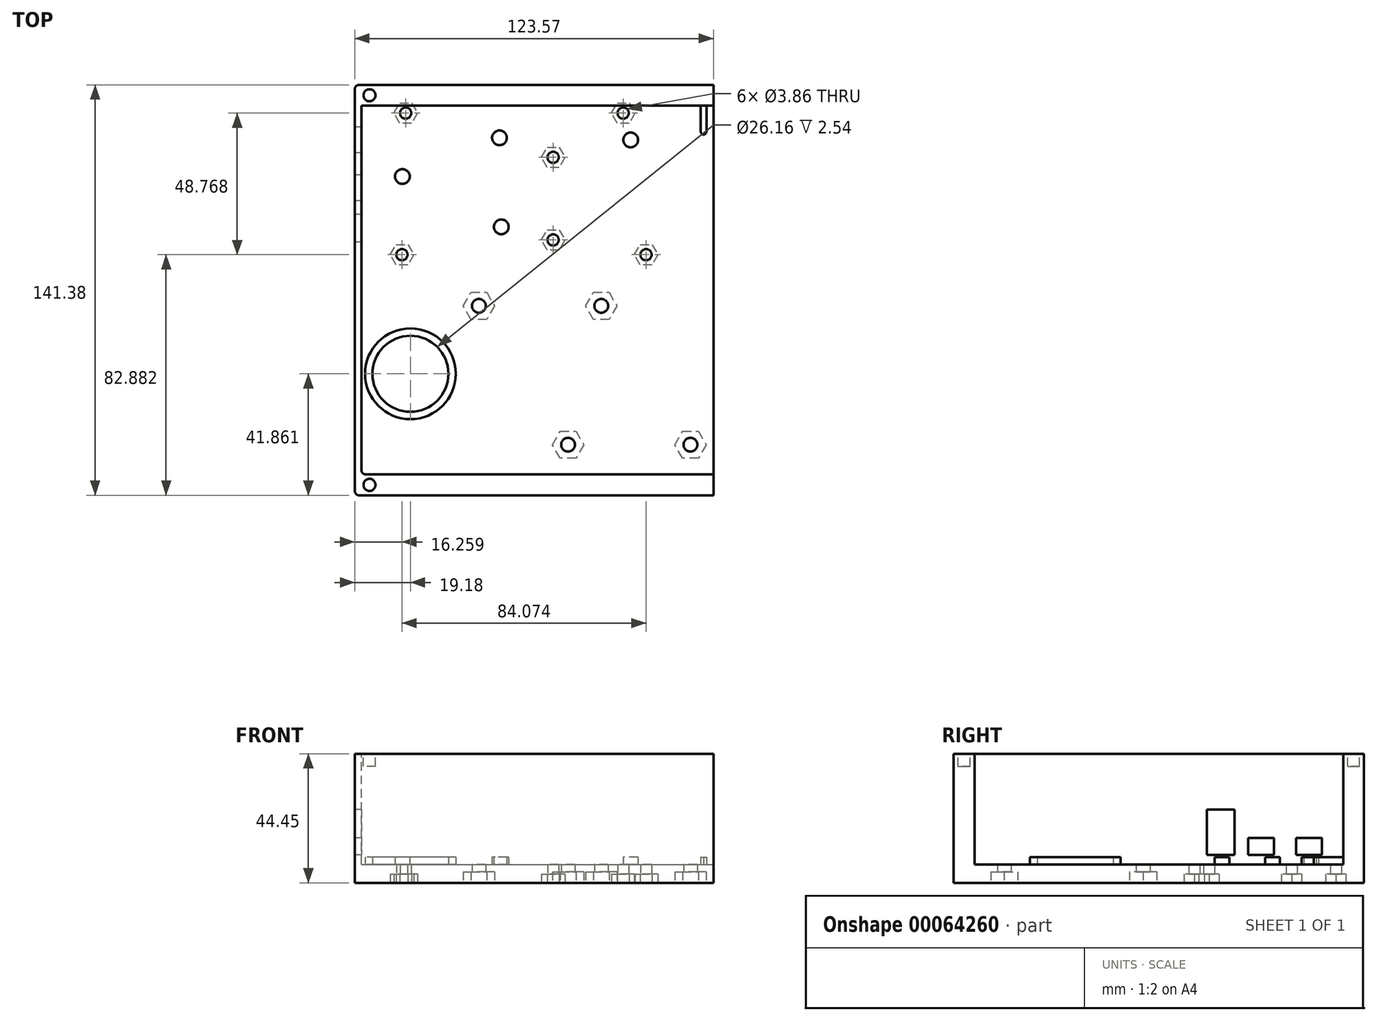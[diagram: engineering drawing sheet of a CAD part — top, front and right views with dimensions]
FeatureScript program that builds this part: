
annotation { "Feature Type Name" : "Feature", "Feature Type Description" : "" }
export const myFeature = defineFeature(function(context is Context, id is Id, definition is map)
    precondition{}
    {
        {
            var Q0;
            Q0=qCreatedBy(makeId("Top.planeOp"),FACE);
            var sketch = newSketch(context, id + "F0", { "sketchPlane" : qUnion([Q0])});
            skLineSegment(sketch, "E0.bottom", {"start": v(-98.88, 40.37) * mm, "end": v(3.23, 40.37) * mm});
            skLineSegment(sketch, "E0.top", {"start": v(-98.88, -13.48) * mm, "end": v(3.23, -13.48) * mm});
            skLineSegment(sketch, "E0.left", {"start": v(-98.88, 40.37) * mm, "end": v(-98.88, -13.48) * mm});
            skLineSegment(sketch, "E0.right", {"start": v(3.23, 40.37) * mm, "end": v(3.23, -13.48) * mm});
            skSolve(sketch);
        }
        {
            var Q0;
            Q0=qCreatedBy(makeId("Top.planeOp"),FACE);
            var sketch = newSketch(context, id + "F1", { "sketchPlane" : qUnion([Q0])});
            skLineSegment(sketch, "E1.bottom", {"start": v(-98.88, 40.37) * mm, "end": v(88.57, 40.37) * mm});
            skLineSegment(sketch, "E1.top", {"start": v(-98.88, -86.63) * mm, "end": v(88.57, -86.63) * mm});
            skLineSegment(sketch, "E1.left", {"start": v(-98.88, 40.37) * mm, "end": v(-98.88, -86.63) * mm});
            skLineSegment(sketch, "E1.right", {"start": v(88.57, 40.37) * mm, "end": v(88.57, -86.63) * mm});
            skSolve(sketch);
        }
        {
            var Q0;
            Q0=qCreatedBy(makeId("Top.planeOp"),FACE);
            var sketch = newSketch(context, id + "F2", { "sketchPlane" : qUnion([Q0])});
            skLineSegment(sketch, "E2", {"start": v(5.77, 40.37) * mm, "end": v(5.77, 30.21) * mm});
            skLineSegment(sketch, "E3", {"start": v(5.77, 30.21) * mm, "end": v(3.23, 30.21) * mm});
            skLineSegment(sketch, "E4", {"start": v(3.23, 30.21) * mm, "end": v(3.23, 40.37) * mm});
            skLineSegment(sketch, "E5", {"start": v(3.23, -3.32) * mm, "end": v(5.77, -3.32) * mm});
            skLineSegment(sketch, "E6", {"start": v(5.77, -3.32) * mm, "end": v(5.77, -16.02) * mm});
            skLineSegment(sketch, "E7", {"start": v(5.77, -16.02) * mm, "end": v(-6.93, -16.02) * mm});
            skLineSegment(sketch, "E8", {"start": v(-6.93, -16.02) * mm, "end": v(-6.93, -13.48) * mm});
            skLineSegment(sketch, "E9", {"start": v(-6.93, -13.48) * mm, "end": v(3.23, -13.48) * mm});
            skLineSegment(sketch, "E10", {"start": v(3.23, -13.48) * mm, "end": v(3.23, -3.32) * mm});
            skLineSegment(sketch, "E11", {"start": v(-6.93, -16.02) * mm, "end": v(-98.88, -16.02) * mm, "construction": true});
            skLineSegment(sketch, "E12", {"start": v(3.23, 40.37) * mm, "end": v(5.77, 40.37) * mm});
            skSolve(sketch);
        }
        {
            var Q0;
            Q0=qCreatedBy(makeId("Top.planeOp"),FACE);
            var sketch = newSketch(context, id + "F3", { "sketchPlane" : qUnion([Q0])});
            skCircle(sketch, "E13", {"center": v(-84.91, -10.94) * mm, "radius": 1.93 * mm});
            skCircle(sketch, "E14", {"center": v(-32.84, -5.86) * mm, "radius": 1.93 * mm});
            skCircle(sketch, "E15", {"center": v(-32.84, 22.6) * mm, "radius": 1.93 * mm});
            skCircle(sketch, "E16", {"center": v(-8.71, 37.83) * mm, "radius": 1.93 * mm});
            skCircle(sketch, "E17", {"center": v(-83.64, 37.83) * mm, "radius": 1.93 * mm});
            skCircle(sketch, "E18", {"center": v(-0.84, -10.94) * mm, "radius": 1.93 * mm});
            skLineSegment(sketch, "E19", {"start": v(-32.84, 40.38) * mm, "end": v(-32.84, -13.48) * mm, "construction": true});
            skLineSegment(sketch, "E20", {"start": v(-32.84, 22.6) * mm, "end": v(3.23, 22.6) * mm, "construction": true});
            skSolve(sketch);
        }
        {
            var Q0;
            Q0=qCreatedBy(makeId("Top.planeOp"),FACE);
            var sketch = newSketch(context, id + "F4", { "sketchPlane" : qUnion([Q0])});
            skCircle(sketch, "E21", {"center": v(-81.99, -51.96) * mm, "radius": 13.08 * mm});
            skCircle(sketch, "E22", {"center": v(-81.99, -51.96) * mm, "radius": 15.62 * mm});
            skSolve(sketch);
        }
        {
            var Q0;
            Q0=qCreatedBy(makeId("Top.planeOp"),FACE);
            var sketch = newSketch(context, id + "F5", { "sketchPlane" : qUnion([Q0])});
            skLineSegment(sketch, "E23.bottom", {"start": v(-101.17, 47.56) * mm, "end": v(91.62, 47.56) * mm});
            skLineSegment(sketch, "E23.top", {"start": v(-101.17, -93.82) * mm, "end": v(91.62, -93.82) * mm});
            skLineSegment(sketch, "E23.left", {"start": v(-101.17, 47.56) * mm, "end": v(-101.17, -93.82) * mm});
            skLineSegment(sketch, "E23.right", {"start": v(91.62, 47.56) * mm, "end": v(91.62, -93.82) * mm});
            skSolve(sketch);
        }
        {
            var Q0;
            Q0=makeQuery(id+"F5.imprint","IMPRINT",FACE,{"disambiguationData":[TD([[makeQuery(id+"F5.imprint","IMPRINT",EDGE,{"derivedFrom":sQuery(id+"F5.wireOp",EDGE,"E23.bottom")}),-1.0]])]});
            var sketch = newSketch(context, id + "F6", { "sketchPlane" : qUnion([Q0])});
            skCircle(sketch, "E24.cCircle", {"center": v(-83.64, 37.83) * mm, "radius": 3.5 * mm, "construction": true});
            skLineSegment(sketch, "E24.0", {"start": v(-79.6, 37.83) * mm, "end": v(-81.62, 34.34) * mm});
            skLineSegment(sketch, "E24.1", {"start": v(-81.62, 34.34) * mm, "end": v(-85.66, 34.34) * mm});
            skLineSegment(sketch, "E24.2", {"start": v(-85.66, 34.34) * mm, "end": v(-87.67, 37.83) * mm});
            skLineSegment(sketch, "E24.3", {"start": v(-87.67, 37.83) * mm, "end": v(-85.66, 41.32) * mm});
            skLineSegment(sketch, "E24.4", {"start": v(-85.66, 41.32) * mm, "end": v(-81.62, 41.32) * mm});
            skLineSegment(sketch, "E24.5", {"start": v(-81.62, 41.32) * mm, "end": v(-79.6, 37.83) * mm});
            skPoint(sketch, "E24.0.midPoint", {"position": v(-80.62, 36.08) * mm});
            skCircle(sketch, "E25.cCircle", {"center": v(-8.71, 37.83) * mm, "radius": 3.5 * mm, "construction": true});
            skLineSegment(sketch, "E25.0", {"start": v(-4.68, 37.83) * mm, "end": v(-6.7, 34.34) * mm});
            skLineSegment(sketch, "E25.1", {"start": v(-6.7, 34.34) * mm, "end": v(-10.73, 34.34) * mm});
            skLineSegment(sketch, "E25.2", {"start": v(-10.73, 34.34) * mm, "end": v(-12.74, 37.83) * mm});
            skLineSegment(sketch, "E25.3", {"start": v(-12.74, 37.83) * mm, "end": v(-10.73, 41.32) * mm});
            skLineSegment(sketch, "E25.4", {"start": v(-10.73, 41.32) * mm, "end": v(-6.7, 41.32) * mm});
            skLineSegment(sketch, "E25.5", {"start": v(-6.7, 41.32) * mm, "end": v(-4.68, 37.83) * mm});
            skPoint(sketch, "E25.0.midPoint", {"position": v(-5.69, 36.08) * mm});
            skCircle(sketch, "E26.cCircle", {"center": v(-32.84, 22.6) * mm, "radius": 3.5 * mm, "construction": true});
            skLineSegment(sketch, "E26.0", {"start": v(-28.8, 22.6) * mm, "end": v(-30.82, 19.1) * mm});
            skLineSegment(sketch, "E26.1", {"start": v(-30.82, 19.1) * mm, "end": v(-34.86, 19.1) * mm});
            skLineSegment(sketch, "E26.2", {"start": v(-34.86, 19.1) * mm, "end": v(-36.87, 22.6) * mm});
            skLineSegment(sketch, "E26.3", {"start": v(-36.87, 22.6) * mm, "end": v(-34.86, 26.08) * mm});
            skLineSegment(sketch, "E26.4", {"start": v(-34.86, 26.08) * mm, "end": v(-30.82, 26.08) * mm});
            skLineSegment(sketch, "E26.5", {"start": v(-30.82, 26.08) * mm, "end": v(-28.8, 22.6) * mm});
            skPoint(sketch, "E26.0.midPoint", {"position": v(-29.82, 20.84) * mm});
            skCircle(sketch, "E27.cCircle", {"center": v(-84.91, -10.94) * mm, "radius": 3.5 * mm, "construction": true});
            skLineSegment(sketch, "E27.0", {"start": v(-80.88, -10.94) * mm, "end": v(-82.9, -14.43) * mm});
            skLineSegment(sketch, "E27.1", {"start": v(-82.9, -14.43) * mm, "end": v(-86.93, -14.43) * mm});
            skLineSegment(sketch, "E27.2", {"start": v(-86.93, -14.43) * mm, "end": v(-88.94, -10.94) * mm});
            skLineSegment(sketch, "E27.3", {"start": v(-88.94, -10.94) * mm, "end": v(-86.93, -7.45) * mm});
            skLineSegment(sketch, "E27.4", {"start": v(-86.93, -7.45) * mm, "end": v(-82.9, -7.45) * mm});
            skLineSegment(sketch, "E27.5", {"start": v(-82.9, -7.45) * mm, "end": v(-80.88, -10.94) * mm});
            skPoint(sketch, "E27.0.midPoint", {"position": v(-81.89, -12.68) * mm});
            skCircle(sketch, "E28.cCircle", {"center": v(-32.84, -5.86) * mm, "radius": 3.5 * mm, "construction": true});
            skLineSegment(sketch, "E28.0", {"start": v(-28.8, -5.86) * mm, "end": v(-30.82, -9.35) * mm});
            skLineSegment(sketch, "E28.1", {"start": v(-30.82, -9.35) * mm, "end": v(-34.86, -9.35) * mm});
            skLineSegment(sketch, "E28.2", {"start": v(-34.86, -9.35) * mm, "end": v(-36.87, -5.86) * mm});
            skLineSegment(sketch, "E28.3", {"start": v(-36.87, -5.86) * mm, "end": v(-34.86, -2.37) * mm});
            skLineSegment(sketch, "E28.4", {"start": v(-34.86, -2.37) * mm, "end": v(-30.82, -2.37) * mm});
            skLineSegment(sketch, "E28.5", {"start": v(-30.82, -2.37) * mm, "end": v(-28.8, -5.86) * mm});
            skPoint(sketch, "E28.0.midPoint", {"position": v(-29.82, -7.6) * mm});
            skCircle(sketch, "E29.cCircle", {"center": v(-0.84, -10.94) * mm, "radius": 3.5 * mm, "construction": true});
            skLineSegment(sketch, "E29.0", {"start": v(3.2, -10.94) * mm, "end": v(1.18, -14.43) * mm});
            skLineSegment(sketch, "E29.1", {"start": v(1.18, -14.43) * mm, "end": v(-2.85, -14.43) * mm});
            skLineSegment(sketch, "E29.2", {"start": v(-2.85, -14.43) * mm, "end": v(-4.87, -10.94) * mm});
            skLineSegment(sketch, "E29.3", {"start": v(-4.87, -10.94) * mm, "end": v(-2.85, -7.45) * mm});
            skLineSegment(sketch, "E29.4", {"start": v(-2.85, -7.45) * mm, "end": v(1.18, -7.45) * mm});
            skLineSegment(sketch, "E29.5", {"start": v(1.18, -7.45) * mm, "end": v(3.2, -10.94) * mm});
            skPoint(sketch, "E29.0.midPoint", {"position": v(2.19, -12.68) * mm});
            skSolve(sketch);
        }
        {
            var Q0;
            Q0=qSketchRegion(id+"F5",true);
            extrude(context, id + "F7", {"entities" : qUnion([Q0]), "depth" : 44.45 * mm, "offsetDistance" : 25.4 * mm});
        }
        {
            var Q0;
            {var subQ25=sQuery(id+"F5.wireOp",EDGE,"E23.bottom");var subQ26=makeQuery(id+"F7.opExtrude","SWEPT_FACE",FACE,{"disambiguationData":[OSD([subQ25])]});var subQ30=sQuery(id+"F5.wireOp",EDGE,"E23.right");var subQ34=sQuery(id+"F5.wireOp",EDGE,"E23.top");var subQ38=sQuery(id+"F5.wireOp",EDGE,"E23.left");Q0=makeQuery(id+"F15.boolean.opBoolean","SPLIT",FACE,{"disambiguationData":[TD([subQ26])],"derivedFrom":makeQuery(id+"FjWOXJXr2Yc3tZQ_1.boolean.opBoolean","SPLIT",FACE,{"disambiguationData":[TD([subQ26])],"derivedFrom":makeQuery(id+"F7.opExtrude","CAP_FACE",FACE,{"disambiguationData":[OSD([subQ25,subQ34,subQ38,subQ30])],"isStart":false})})});}
            var sketch = newSketch(context, id + "F8", { "sketchPlane" : qUnion([Q0])});
            skLineSegment(sketch, "E30.bottom", {"start": v(-98.88, 40.37) * mm, "end": v(3.23, 40.37) * mm});
            skLineSegment(sketch, "E30.top", {"start": v(-98.88, -13.48) * mm, "end": v(3.23, -13.48) * mm});
            skLineSegment(sketch, "E30.left", {"start": v(-98.88, 40.37) * mm, "end": v(-98.88, -13.48) * mm});
            skLineSegment(sketch, "E30.right", {"start": v(3.23, 40.37) * mm, "end": v(3.23, -13.48) * mm});
            skSolve(sketch);
        }
        {
            var Q0;
            Q0=qCreatedBy(makeId("Top.planeOp"),FACE);
            var sketch = newSketch(context, id + "F9", { "sketchPlane" : qUnion([Q0])});
            skCircle(sketch, "E31.cCircle", {"center": v(-58.43, -28.57) * mm, "radius": 4.67 * mm, "construction": true});
            skLineSegment(sketch, "E31.0", {"start": v(-53.04, -28.57) * mm, "end": v(-55.73, -33.24) * mm});
            skLineSegment(sketch, "E31.1", {"start": v(-55.73, -33.24) * mm, "end": v(-61.13, -33.24) * mm});
            skLineSegment(sketch, "E31.2", {"start": v(-61.13, -33.24) * mm, "end": v(-63.83, -28.57) * mm});
            skLineSegment(sketch, "E31.3", {"start": v(-63.83, -28.57) * mm, "end": v(-61.13, -23.9) * mm});
            skLineSegment(sketch, "E31.4", {"start": v(-61.13, -23.9) * mm, "end": v(-55.73, -23.9) * mm});
            skLineSegment(sketch, "E31.5", {"start": v(-55.73, -23.9) * mm, "end": v(-53.04, -28.57) * mm});
            skPoint(sketch, "E31.0.midPoint", {"position": v(-54.38, -30.9) * mm});
            skCircle(sketch, "E32.cCircle", {"center": v(-27.7, -76.4) * mm, "radius": 4.67 * mm, "construction": true});
            skLineSegment(sketch, "E32.0", {"start": v(-22.3, -76.4) * mm, "end": v(-25, -81.07) * mm});
            skLineSegment(sketch, "E32.1", {"start": v(-25, -81.07) * mm, "end": v(-30.4, -81.07) * mm});
            skLineSegment(sketch, "E32.2", {"start": v(-30.4, -81.07) * mm, "end": v(-33.1, -76.4) * mm});
            skLineSegment(sketch, "E32.3", {"start": v(-33.1, -76.4) * mm, "end": v(-30.4, -71.72) * mm});
            skLineSegment(sketch, "E32.4", {"start": v(-30.4, -71.72) * mm, "end": v(-25, -71.72) * mm});
            skLineSegment(sketch, "E32.5", {"start": v(-25, -71.72) * mm, "end": v(-22.3, -76.4) * mm});
            skPoint(sketch, "E32.0.midPoint", {"position": v(-23.65, -78.73) * mm});
            skCircle(sketch, "E33.cCircle", {"center": v(-16.27, -28.57) * mm, "radius": 4.67 * mm, "construction": true});
            skLineSegment(sketch, "E33.0", {"start": v(-13.57, -23.9) * mm, "end": v(-10.87, -28.57) * mm});
            skLineSegment(sketch, "E33.1", {"start": v(-10.87, -28.57) * mm, "end": v(-13.57, -33.24) * mm});
            skLineSegment(sketch, "E33.2", {"start": v(-13.57, -33.24) * mm, "end": v(-18.97, -33.24) * mm});
            skLineSegment(sketch, "E33.3", {"start": v(-18.97, -33.24) * mm, "end": v(-21.66, -28.57) * mm});
            skLineSegment(sketch, "E33.4", {"start": v(-21.66, -28.57) * mm, "end": v(-18.97, -23.9) * mm});
            skLineSegment(sketch, "E33.5", {"start": v(-18.97, -23.9) * mm, "end": v(-13.57, -23.9) * mm});
            skPoint(sketch, "E33.0.midPoint", {"position": v(-12.22, -26.23) * mm});
            skCircle(sketch, "E34.cCircle", {"center": v(14.47, -76.4) * mm, "radius": 4.67 * mm, "construction": true});
            skLineSegment(sketch, "E34.0", {"start": v(17.16, -71.72) * mm, "end": v(19.86, -76.4) * mm});
            skLineSegment(sketch, "E34.1", {"start": v(19.86, -76.4) * mm, "end": v(17.16, -81.07) * mm});
            skLineSegment(sketch, "E34.2", {"start": v(17.16, -81.07) * mm, "end": v(11.77, -81.07) * mm});
            skLineSegment(sketch, "E34.3", {"start": v(11.77, -81.07) * mm, "end": v(9.07, -76.4) * mm});
            skLineSegment(sketch, "E34.4", {"start": v(9.07, -76.4) * mm, "end": v(11.77, -71.72) * mm});
            skLineSegment(sketch, "E34.5", {"start": v(11.77, -71.72) * mm, "end": v(17.16, -71.72) * mm});
            skPoint(sketch, "E34.0.midPoint", {"position": v(18.51, -74.06) * mm});
            skLineSegment(sketch, "E35", {"start": v(-58.43, -28.57) * mm, "end": v(-27.7, -28.57) * mm, "construction": true});
            skLineSegment(sketch, "E36", {"start": v(-27.7, -28.57) * mm, "end": v(-27.7, -76.4) * mm, "construction": true});
            skLineSegment(sketch, "E37", {"start": v(-16.27, -28.57) * mm, "end": v(14.47, -28.57) * mm});
            skLineSegment(sketch, "E38", {"start": v(14.47, -76.4) * mm, "end": v(14.47, -28.57) * mm});
            skLineSegment(sketch, "E39", {"start": v(-66.37, -20.88) * mm, "end": v(-66.37, -51.5) * mm, "construction": true});
            skSolve(sketch);
        }
        {
            var Q0;
            Q0=qCreatedBy(makeId("Top.planeOp"),FACE);
            var sketch = newSketch(context, id + "F10", { "sketchPlane" : qUnion([Q0])});
            skCircle(sketch, "E40", {"center": v(-58.43, -28.57) * mm, "radius": 2.37 * mm});
            skCircle(sketch, "E41", {"center": v(-27.7, -76.4) * mm, "radius": 2.37 * mm});
            skCircle(sketch, "E42", {"center": v(-16.27, -28.57) * mm, "radius": 2.37 * mm});
            skCircle(sketch, "E43", {"center": v(14.47, -76.4) * mm, "radius": 2.37 * mm});
            skSolve(sketch);
        }
        {
            var Q0;
            Q0=qCreatedBy(makeId("Top.planeOp"),FACE);
            var sketch = newSketch(context, id + "F11", { "sketchPlane" : qUnion([Q0])});
            skCircle(sketch, "E44", {"center": v(-6.14, 28.58) * mm, "radius": 2.54 * mm});
            skCircle(sketch, "E45", {"center": v(-51.31, 29.3) * mm, "radius": 2.54 * mm});
            skCircle(sketch, "E46", {"center": v(-50.7, -1.38) * mm, "radius": 2.54 * mm});
            skCircle(sketch, "E47", {"center": v(-84.77, 15.99) * mm, "radius": 2.54 * mm});
            skSolve(sketch);
        }
        {
            var Q0;
            Q0=makeQuery(id+"F7.opExtrude","CAP_FACE",FACE,{"disambiguationData":[OSD([sQuery(id+"F5.wireOp",EDGE,"E23.bottom"),sQuery(id+"F5.wireOp",EDGE,"E23.top"),sQuery(id+"F5.wireOp",EDGE,"E23.left"),sQuery(id+"F5.wireOp",EDGE,"E23.right")])],"isStart":false});
            var sketch = newSketch(context, id + "F12", { "sketchPlane" : qUnion([Q0])});
            skLineSegment(sketch, "E48.bottom", {"start": v(-98.88, 40.37) * mm, "end": v(88.57, 40.37) * mm});
            skLineSegment(sketch, "E48.top", {"start": v(-98.88, -86.63) * mm, "end": v(88.57, -86.63) * mm});
            skLineSegment(sketch, "E48.left", {"start": v(-98.88, 40.37) * mm, "end": v(-98.88, -86.63) * mm});
            skLineSegment(sketch, "E48.right", {"start": v(88.57, 40.37) * mm, "end": v(88.57, -86.63) * mm});
            skSolve(sketch);
        }
        {
            var Q0;
            Q0=qCreatedBy(makeId("Top.planeOp"),FACE);
            var sketch = newSketch(context, id + "F13", { "sketchPlane" : qUnion([Q0])});
            skLineSegment(sketch, "E49", {"start": v(17.96, 30.21) * mm, "end": v(20, 30.21) * mm});
            skLineSegment(sketch, "E50", {"start": v(17.96, 40.37) * mm, "end": v(17.96, 30.21) * mm});
            skLineSegment(sketch, "E51", {"start": v(52.73, -26.81) * mm, "end": v(52.73, -24.78) * mm});
            skLineSegment(sketch, "E52", {"start": v(52.73, -24.78) * mm, "end": v(42.57, -24.78) * mm});
            skLineSegment(sketch, "E53", {"start": v(20, 40.37) * mm, "end": v(20, 30.21) * mm});
            skLineSegment(sketch, "E54", {"start": v(17.96, 40.37) * mm, "end": v(20, 40.37) * mm});
            skLineSegment(sketch, "E55", {"start": v(42.57, -24.78) * mm, "end": v(42.57, -26.81) * mm});
            skLineSegment(sketch, "E56", {"start": v(42.57, -26.81) * mm, "end": v(52.73, -26.81) * mm});
            skLineSegment(sketch, "E57", {"start": v(20, 40.37) * mm, "end": v(20, -85.45) * mm});
            skSolve(sketch);
        }
        {
            var Q0;
            Q0=qSketchRegion(id+"F12",true);
            extrude(context, id + "F14", {"entities" : qUnion([Q0]), "operationType" : NewBodyOperationType.REMOVE, "oppositeDirection" : true, "depth" : 38.1 * mm, "offsetDistance" : 25.4 * mm});
        }
        {
            var Q0;
            Q0=qSketchRegion(id+"F4",true);
            var Q1;
            Q1=qSketchRegion(id+"F13",true);
            extrude(context, id + "F15", {"entities" : qUnion([Q0, Q1]), "operationType" : NewBodyOperationType.ADD, "depth" : 8.9 * mm, "offsetDistance" : 25.4 * mm});
        }
        {
            var Q0;
            Q0=qSketchRegion(id+"F6",true);
            extrude(context, id + "F16", {"entities" : qUnion([Q0]), "operationType" : NewBodyOperationType.REMOVE, "depth" : 3 * mm, "offsetDistance" : 25.4 * mm});
        }
        {
            var Q0;
            Q0=qSketchRegion(id+"F9",true);
            extrude(context, id + "F17", {"entities" : qUnion([Q0]), "operationType" : NewBodyOperationType.REMOVE, "depth" : 3.8 * mm, "offsetDistance" : 25.4 * mm});
        }
        {
            var Q0;
            Q0=qSketchRegion(id+"F10",true);
            extrude(context, id + "F18", {"entities" : qUnion([Q0]), "operationType" : NewBodyOperationType.REMOVE, "depth" : 25.4 * mm, "offsetDistance" : 25.4 * mm});
        }
        {
            var Q0;
            Q0=qSketchRegion(id+"F3",true);
            extrude(context, id + "F19", {"entities" : qUnion([Q0]), "operationType" : NewBodyOperationType.REMOVE, "depth" : 25.4 * mm, "offsetDistance" : 25.4 * mm});
        }
        {
            var Q0;
            Q0=qSketchRegion(id+"F11",true);
            extrude(context, id + "F20", {"entities" : qUnion([Q0]), "operationType" : NewBodyOperationType.ADD, "depth" : 8.9 * mm, "offsetDistance" : 25.4 * mm});
        }
        {
            var Q0;
            Q0=makeQuery(id+"F7.opExtrude","SWEPT_FACE",FACE,{"disambiguationData":[OSD([sQuery(id+"F5.wireOp",EDGE,"E23.left")])]});
            var sketch = newSketch(context, id + "F21", { "sketchPlane" : qUnion([Q0])});
            skLineSegment(sketch, "E58", {"start": v(-47.56, 6.35) * mm, "end": v(93.82, 6.35) * mm, "construction": true});
            skLineSegment(sketch, "E59", {"start": v(-43.75, 44.45) * mm, "end": v(-43.75, 0) * mm, "construction": true});
            skLineSegment(sketch, "E60", {"start": v(-47.56, 9.65) * mm, "end": v(93.82, 9.65) * mm, "construction": true});
            skLineSegment(sketch, "E61", {"start": v(-7.68, 15.5) * mm, "end": v(-7.68, 9.65) * mm});
            skLineSegment(sketch, "E62", {"start": v(-7.68, 9.65) * mm, "end": v(-16.57, 9.65) * mm});
            skLineSegment(sketch, "E63", {"start": v(-16.57, 9.65) * mm, "end": v(-16.57, 15.5) * mm});
            skLineSegment(sketch, "E64", {"start": v(10.1, 15.5) * mm, "end": v(10.1, 9.65) * mm, "construction": true});
            skLineSegment(sketch, "E65", {"start": v(-24.2, 15.5) * mm, "end": v(-24.2, 9.65) * mm});
            skLineSegment(sketch, "E66", {"start": v(-24.2, 9.65) * mm, "end": v(-33.08, 9.65) * mm});
            skLineSegment(sketch, "E67", {"start": v(-33.08, 9.65) * mm, "end": v(-33.08, 15.5) * mm});
            skLineSegment(sketch, "E68", {"start": v(-33.08, 15.5) * mm, "end": v(-24.2, 15.5) * mm});
            skLineSegment(sketch, "E69", {"start": v(-16.57, 15.5) * mm, "end": v(-7.68, 15.5) * mm});
            skLineSegment(sketch, "E70", {"start": v(10.1, 15.5) * mm, "end": v(-47.56, 15.5) * mm, "construction": true});
            skLineSegment(sketch, "E71", {"start": v(6.54, 25.27) * mm, "end": v(6.54, 9.65) * mm});
            skLineSegment(sketch, "E72", {"start": v(-2.98, 9.65) * mm, "end": v(6.54, 9.65) * mm});
            skLineSegment(sketch, "E73", {"start": v(-2.98, 9.65) * mm, "end": v(-2.98, 25.27) * mm});
            skLineSegment(sketch, "E74", {"start": v(-2.98, 25.27) * mm, "end": v(6.54, 25.27) * mm});
            skSolve(sketch);
        }
        {
            var Q0;
            Q0=qSketchRegion(id+"F21",true);
            extrude(context, id + "F22", {"entities" : qUnion([Q0]), "operationType" : NewBodyOperationType.REMOVE, "oppositeDirection" : true, "depth" : 25.4 * mm, "offsetDistance" : 25.4 * mm});
        }
        {
            var Q0;
            Q0=makeQuery(id+"F12.imprint","IMPRINT",FACE,{"disambiguationData":[TD([[makeQuery(id+"F12.imprint","IMPRINT",EDGE,{"derivedFrom":sQuery(id+"F12.wireOp",EDGE,"E48.bottom")}),1.0]])]});
            var sketch = newSketch(context, id + "F23", { "sketchPlane" : qUnion([Q0])});
            skCircle(sketch, "E75", {"center": v(-96.09, -90.22) * mm, "radius": 2.08 * mm});
            skCircle(sketch, "E76", {"center": v(86.54, -90.22) * mm, "radius": 2.08 * mm});
            skCircle(sketch, "E77", {"center": v(86.54, 43.96) * mm, "radius": 2.08 * mm});
            skCircle(sketch, "E78", {"center": v(-96.09, 43.96) * mm, "radius": 2.08 * mm});
            skSolve(sketch);
        }
        {
            var Q0;
            Q0=qSketchRegion(id+"F23",true);
            extrude(context, id + "F24", {"entities" : qUnion([Q0]), "operationType" : NewBodyOperationType.REMOVE, "oppositeDirection" : true, "depth" : 4.32 * mm, "offsetDistance" : 25.4 * mm});
        }
        {
            var Q0;
            Q0=makeQuery(id+"F7.opExtrude","SWEPT_EDGE",EDGE,{"disambiguationData":[OSD([sQuery(id+"F5.wireOp",EDGE,"E23.bottom"),sQuery(id+"F5.wireOp",EDGE,"E23.left")])]});
            var Q1;
            Q1=makeQuery(id+"F7.opExtrude","SWEPT_EDGE",EDGE,{"disambiguationData":[OSD([sQuery(id+"F5.wireOp",EDGE,"E23.top"),sQuery(id+"F5.wireOp",EDGE,"E23.left")])]});
            var Q2;
            Q2=makeQuery(id+"F7.opExtrude","SWEPT_EDGE",EDGE,{"disambiguationData":[OSD([sQuery(id+"F5.wireOp",EDGE,"E23.top"),sQuery(id+"F5.wireOp",EDGE,"E23.right")])]});
            var Q3;
            Q3=makeQuery(id+"F7.opExtrude","SWEPT_EDGE",EDGE,{"disambiguationData":[OSD([sQuery(id+"F5.wireOp",EDGE,"E23.bottom"),sQuery(id+"F5.wireOp",EDGE,"E23.right")])]});
            var Q4;
            Q4=makeQuery(id+"F15.opExtrude","SWEPT_EDGE",EDGE,{"disambiguationData":[OSD([sQuery(id+"F13.wireOp",EDGE,"E49"),sQuery(id+"F13.wireOp",EDGE,"E50")])]});
            var Q5;
            Q5=makeQuery(id+"F15.opExtrude","SWEPT_EDGE",EDGE,{"disambiguationData":[OSD([sQuery(id+"F13.wireOp",EDGE,"E55"),sQuery(id+"F13.wireOp",EDGE,"E56")])]});
            var Q6;
            Q6=makeQuery(id+"F15.opExtrude","SWEPT_EDGE",EDGE,{"disambiguationData":[OSD([sQuery(id+"F13.wireOp",EDGE,"E52"),sQuery(id+"F13.wireOp",EDGE,"E55")])]});
            var Q7;
            Q7=makeQuery(id+"F15.opExtrude","SWEPT_EDGE",EDGE,{"disambiguationData":[OSD([sQuery(id+"F13.wireOp",EDGE,"E49"),sQuery(id+"F13.wireOp",EDGE,"E57")])]});
            var Q8;
            Q8=makeQuery(id+"F15.opExtrude","SWEPT_EDGE",EDGE,{"disambiguationData":[OSD([sQuery(id+"F13.wireOp",EDGE,"E51"),sQuery(id+"F13.wireOp",EDGE,"E56")])]});
            var Q9;
            Q9=makeQuery(id+"F15.opExtrude","SWEPT_EDGE",EDGE,{"disambiguationData":[OSD([sQuery(id+"F13.wireOp",EDGE,"E51"),sQuery(id+"F13.wireOp",EDGE,"E52")])]});
            var Q10;
            Q10=makeQuery(id+"F14.boolean.opBoolean","COPY",EDGE,{"derivedFrom":makeQuery(id+"F14.opExtrude","SWEPT_EDGE",EDGE,{"disambiguationData":[OSD([sQuery(id+"F12.wireOp",EDGE,"E48.top"),sQuery(id+"F12.wireOp",EDGE,"E48.left")])]})});
            var Q11;
            Q11=makeQuery(id+"F14.boolean.opBoolean","COPY",EDGE,{"derivedFrom":makeQuery(id+"F14.opExtrude","SWEPT_EDGE",EDGE,{"disambiguationData":[OSD([sQuery(id+"F12.wireOp",EDGE,"E48.top"),sQuery(id+"F12.wireOp",EDGE,"E48.right")])]})});
            fillet(context, id + "F25", {"entities" : qUnion([Q0, Q1, Q2, Q3, Q4, Q5, Q6, Q7, Q8, Q9, Q10, Q11]), "radius" : 1.52 * mm, "tangentPropagation" : true, "allowEdgeOverflow" : false});
        }
        {
            var Q0;
            Q0=qCreatedBy(makeId("Top.planeOp"),FACE);
            var sketch = newSketch(context, id + "F26", { "sketchPlane" : qUnion([Q0])});
            skLineSegment(sketch, "E79.bottom", {"start": v(22.4, 47.56) * mm, "end": v(91.62, 47.56) * mm});
            skLineSegment(sketch, "E79.top", {"start": v(22.4, -93.82) * mm, "end": v(91.62, -93.82) * mm});
            skLineSegment(sketch, "E79.left", {"start": v(22.4, 47.56) * mm, "end": v(22.4, -93.82) * mm});
            skLineSegment(sketch, "E79.right", {"start": v(91.62, 47.56) * mm, "end": v(91.62, -93.82) * mm});
            skSolve(sketch);
        }
        {
            var Q0;
            Q0 = qSketchRegion(id + "F26", true);
            extrude(context, id + "F27", {"entities" : qUnion([Q0]), "operationType" : NewBodyOperationType.REMOVE, "depth" : 50.8 * mm, "offsetDistance" : 25.4 * mm});
        }
    });
